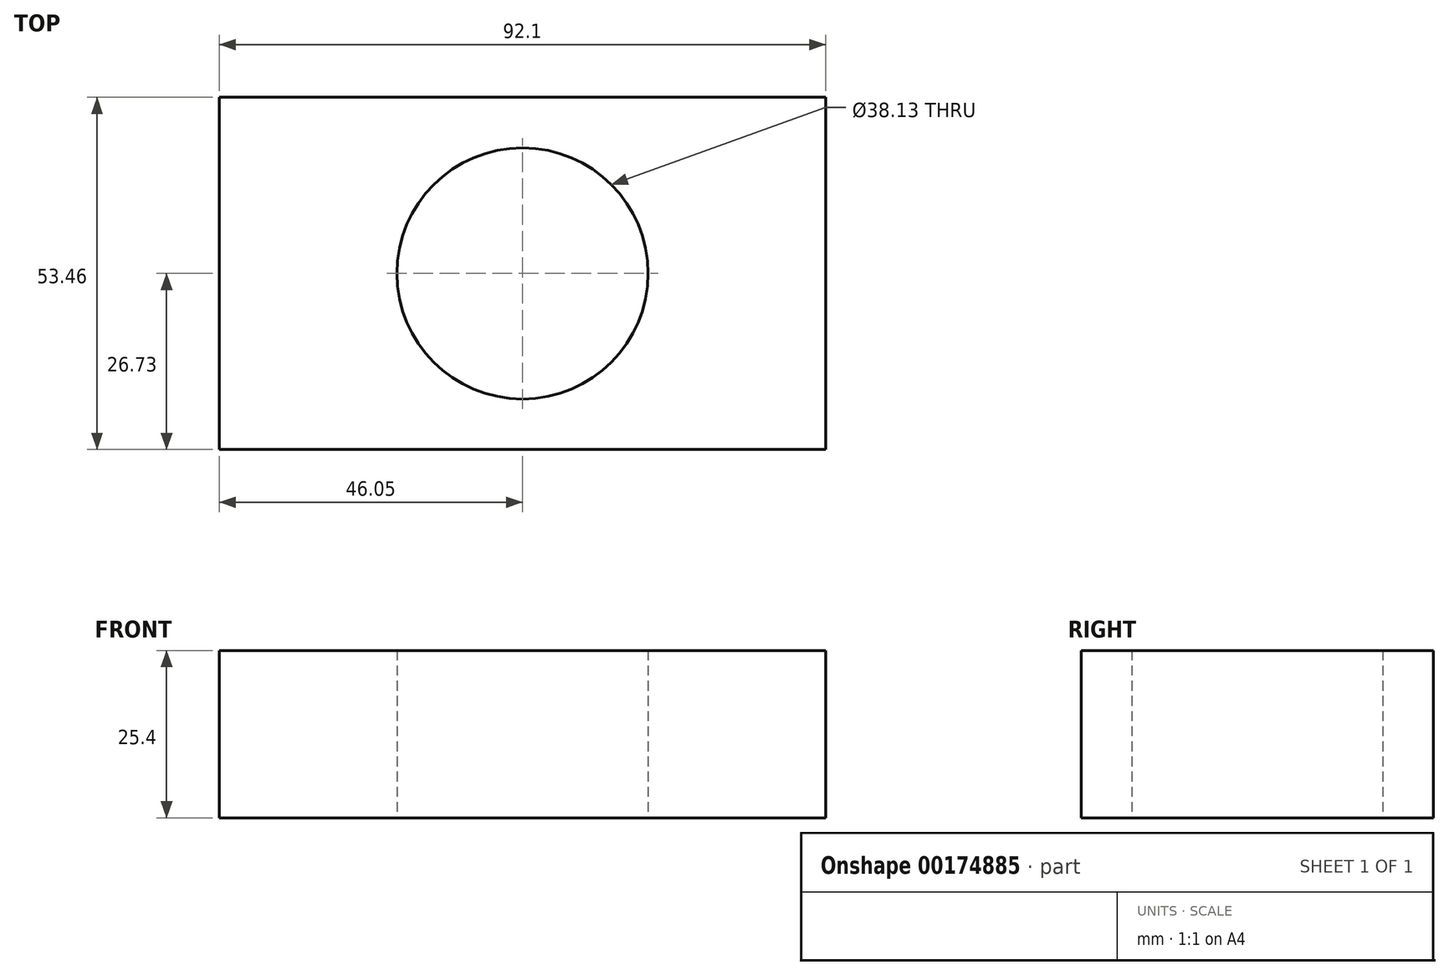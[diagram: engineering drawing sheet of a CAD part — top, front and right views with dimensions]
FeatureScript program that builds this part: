
annotation { "Feature Type Name" : "Feature", "Feature Type Description" : "" }
export const myFeature = defineFeature(function(context is Context, id is Id, definition is map)
    precondition{}
    {
        {
            var Q0;
            Q0=qCreatedBy(makeId("Top.planeOp"),FACE);
            var sketch = newSketch(context, id + "F0", { "sketchPlane" : qUnion([Q0])});
            skLineSegment(sketch, "E0.bottom", {"start": v(46.05, 26.73) * mm, "end": v(-46.05, 26.73) * mm});
            skLineSegment(sketch, "E0.top", {"start": v(46.05, -26.73) * mm, "end": v(-46.05, -26.73) * mm});
            skLineSegment(sketch, "E0.left", {"start": v(46.05, 26.73) * mm, "end": v(46.05, -26.73) * mm});
            skLineSegment(sketch, "E0.right", {"start": v(-46.05, 26.73) * mm, "end": v(-46.05, -26.73) * mm});
            skPoint(sketch, "E0.middle", {"position": v(0, 0) * mm});
            skSolve(sketch);
        }
        {
            var Q0;
            Q0=qSketchRegion(id+"F0",true);
            extrude(context, id + "F1", {"entities" : qUnion([Q0]), "depth" : 25.4 * mm});
        }
        {
            var Q0;
            Q0=sQuery(id+"F0.wireOp",VERTEX,"E0.middle");
            var Q1;
            Q1=makeQuery(id+"F1.opExtrude","SWEPT_BODY",BODY,{"disambiguationData":[OSD([sQuery(id+"F0.wireOp",EDGE,"E0.bottom"),sQuery(id+"F0.wireOp",EDGE,"E0.top"),sQuery(id+"F0.wireOp",EDGE,"E0.left"),sQuery(id+"F0.wireOp",EDGE,"E0.right")])]});
            hole(context, id + "F2", {"style" : HoleStyle.SIMPLE, "endStyle" : HoleEndStyle.THROUGH, "oppositeDirection" : true, "holeDiameter" : 38.13 * mm, "locations" : qUnion([Q0]), "scope" : qUnion([Q1]), "isTappedThrough" : true});
        }
    });
